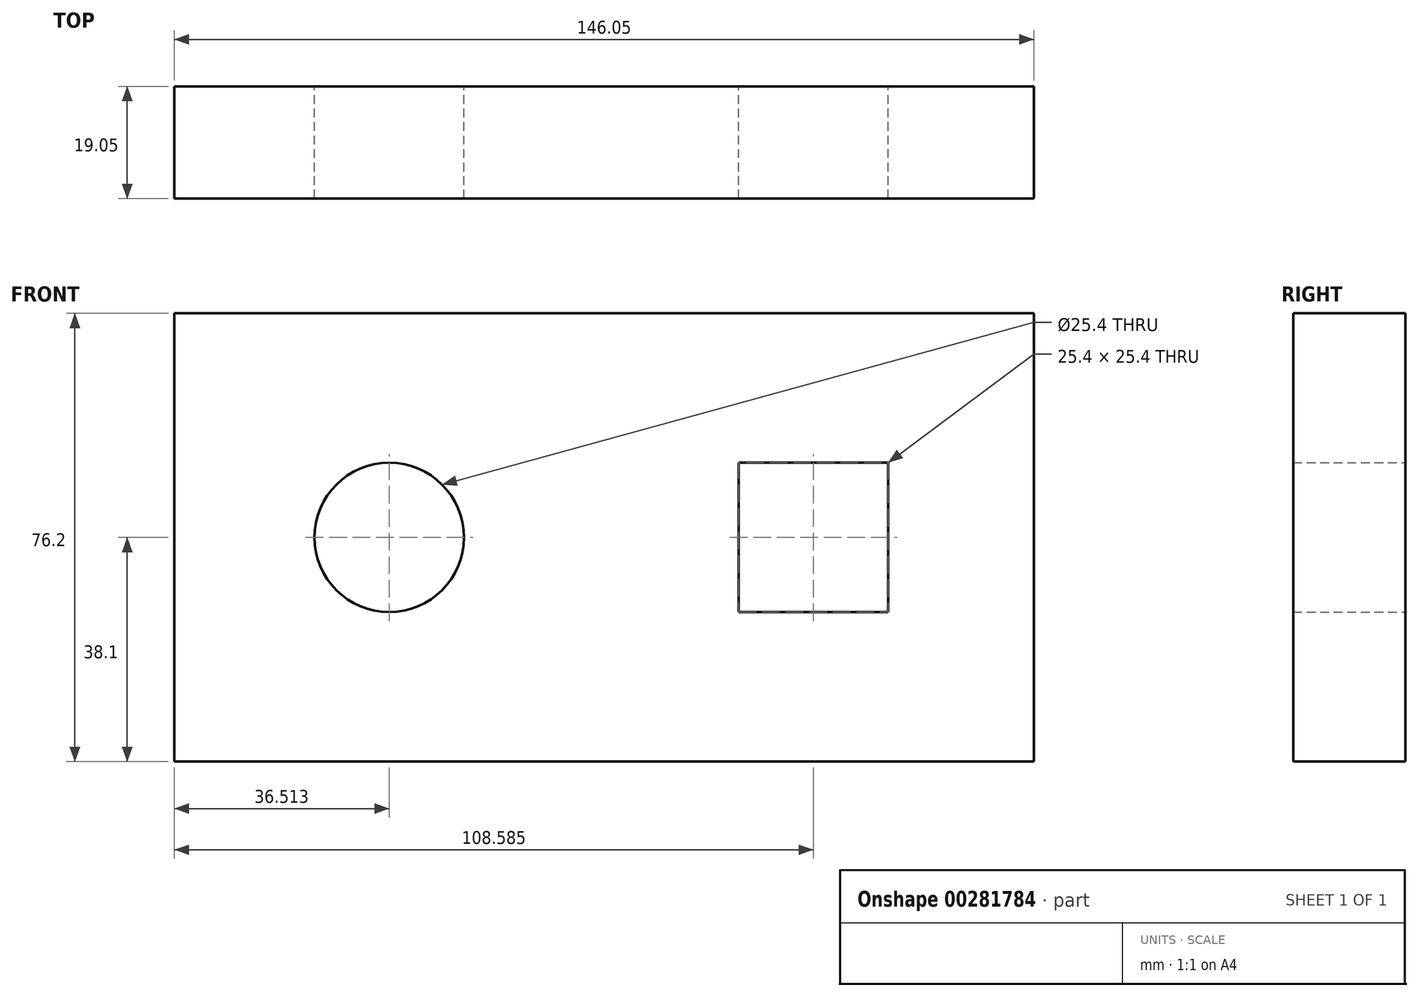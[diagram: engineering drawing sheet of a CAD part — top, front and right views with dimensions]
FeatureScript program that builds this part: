
annotation { "Feature Type Name" : "Feature", "Feature Type Description" : "" }
export const myFeature = defineFeature(function(context is Context, id is Id, definition is map)
    precondition{}
    {
        {
            var Q0;
            Q0=qCreatedBy(makeId("Front.planeOp"),FACE);
            var sketch = newSketch(context, id + "F0", { "sketchPlane" : qUnion([Q0])});
            skLineSegment(sketch, "E0.bottom", {"start": v(0, 0) * mm, "end": v(-146.05, 0) * mm});
            skLineSegment(sketch, "E0.top", {"start": v(0, 76.2) * mm, "end": v(-146.05, 76.2) * mm});
            skLineSegment(sketch, "E0.left", {"start": v(0, 0) * mm, "end": v(0, 76.2) * mm});
            skLineSegment(sketch, "E0.right", {"start": v(-146.05, 0) * mm, "end": v(-146.05, 76.2) * mm});
            skCircle(sketch, "E1", {"center": v(-109.54, 38.1) * mm, "radius": 12.7 * mm});
            skLineSegment(sketch, "E2.bottom", {"start": v(-50.17, 50.8) * mm, "end": v(-24.77, 50.8) * mm});
            skLineSegment(sketch, "E2.top", {"start": v(-50.17, 25.4) * mm, "end": v(-24.77, 25.4) * mm});
            skLineSegment(sketch, "E2.left", {"start": v(-50.17, 50.8) * mm, "end": v(-50.17, 25.4) * mm});
            skLineSegment(sketch, "E2.right", {"start": v(-24.77, 50.8) * mm, "end": v(-24.77, 25.4) * mm});
            skSolve(sketch);
        }
        {
            var Q0;
            Q0 = qSketchRegion(id + "F0", true);
            extrude(context, id + "F1", {"entities" : qUnion([Q0]), "depth" : 19.05 * mm});
        }
    });
